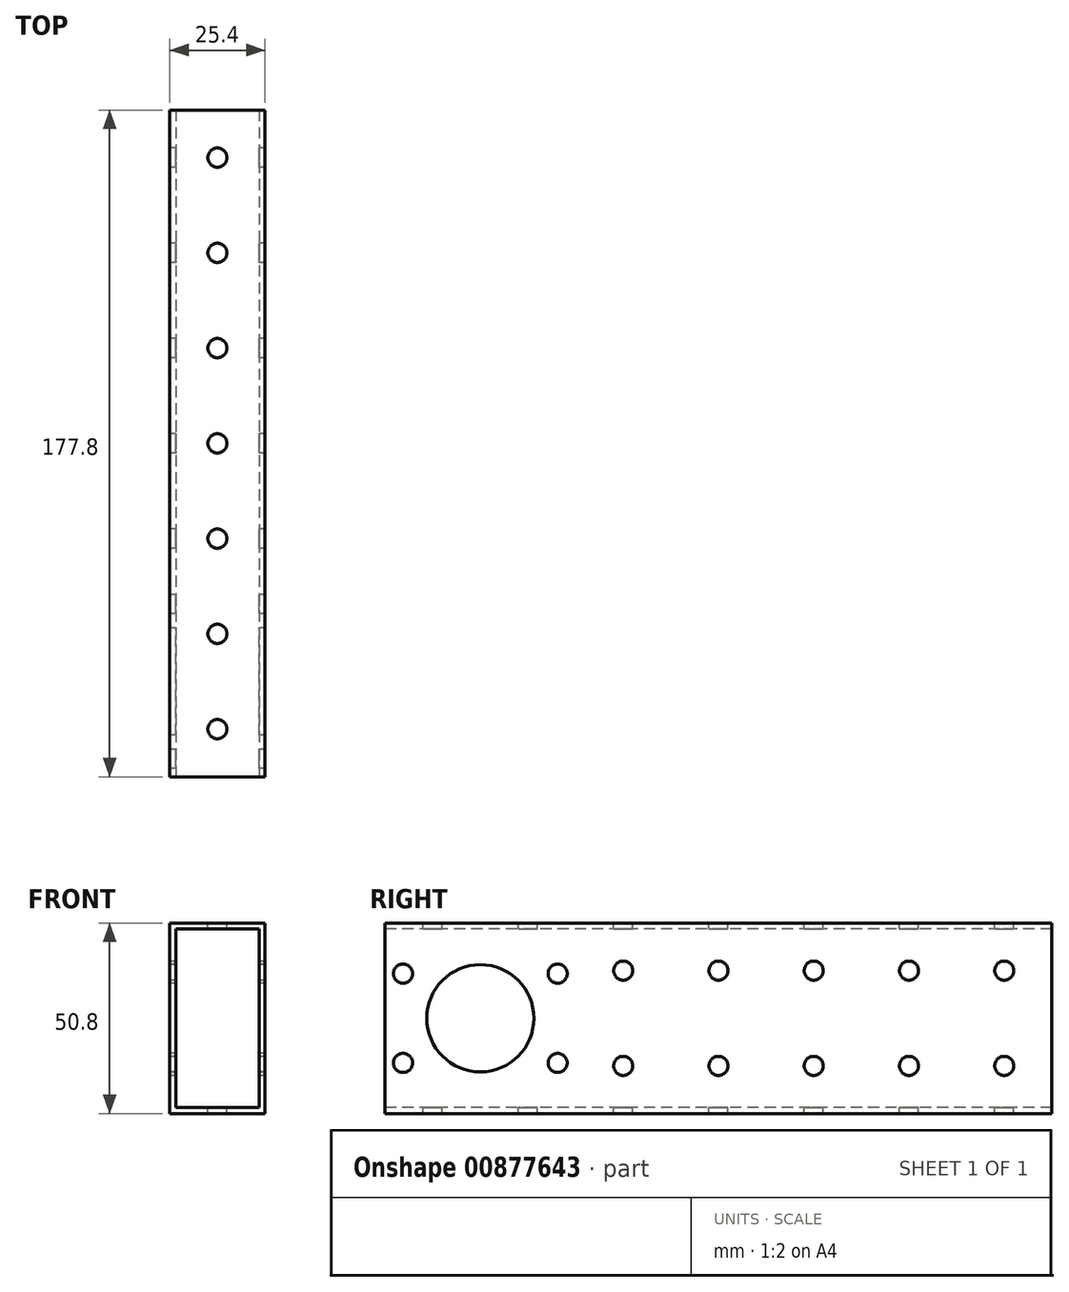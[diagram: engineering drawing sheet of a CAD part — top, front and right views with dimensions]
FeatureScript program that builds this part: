
annotation { "Feature Type Name" : "Feature", "Feature Type Description" : "" }
export const myFeature = defineFeature(function(context is Context, id is Id, definition is map)
    precondition{}
    {
        {
            var Q0;
            Q0=qCreatedBy(makeId("Right.planeOp"),FACE);
            var sketch = newSketch(context, id + "F0", { "sketchPlane" : qUnion([Q0])});
            skLineSegment(sketch, "E0.bottom", {"start": v(-88.9, 25.4) * mm, "end": v(88.9, 25.4) * mm});
            skLineSegment(sketch, "E0.top", {"start": v(-88.9, -25.4) * mm, "end": v(88.9, -25.4) * mm});
            skLineSegment(sketch, "E0.left", {"start": v(-88.9, 25.4) * mm, "end": v(-88.9, -25.4) * mm});
            skLineSegment(sketch, "E0.right", {"start": v(88.9, 25.4) * mm, "end": v(88.9, -25.4) * mm});
            skPoint(sketch, "E0.middle", {"position": v(0, 0) * mm});
            skCircle(sketch, "E1", {"center": v(-63.5, 0) * mm, "radius": 23.81 * mm, "construction": true});
            skCircle(sketch, "E2", {"center": v(-63.5, 23.81) * mm, "radius": 2.55 * mm, "construction": true});
            skCircle(sketch, "E3.1.0", {"center": v(-84.12, 11.9) * mm, "radius": 2.55 * mm});
            skCircle(sketch, "E3.2.0", {"center": v(-84.12, -11.9) * mm, "radius": 2.55 * mm});
            skCircle(sketch, "E3.3.0", {"center": v(-63.5, -23.81) * mm, "radius": 2.55 * mm, "construction": true});
            skCircle(sketch, "E3.4.0", {"center": v(-42.88, -11.9) * mm, "radius": 2.55 * mm});
            skCircle(sketch, "E3.5.0", {"center": v(-42.88, 11.9) * mm, "radius": 2.55 * mm});
            skCircle(sketch, "E4", {"center": v(76.2, 12.7) * mm, "radius": 2.55 * mm});
            skCircle(sketch, "E5.0.1.0", {"center": v(76.2, -12.7) * mm, "radius": 2.55 * mm});
            skCircle(sketch, "E5.1.0.0", {"center": v(50.8, 12.7) * mm, "radius": 2.55 * mm});
            skCircle(sketch, "E5.1.1.0", {"center": v(50.8, -12.7) * mm, "radius": 2.55 * mm});
            skCircle(sketch, "E5.2.0.0", {"center": v(25.4, 12.7) * mm, "radius": 2.55 * mm});
            skCircle(sketch, "E5.2.1.0", {"center": v(25.4, -12.7) * mm, "radius": 2.55 * mm});
            skCircle(sketch, "E5.3.0.0", {"center": v(0, 12.7) * mm, "radius": 2.55 * mm});
            skCircle(sketch, "E5.3.1.0", {"center": v(0, -12.7) * mm, "radius": 2.55 * mm});
            skCircle(sketch, "E5.4.0.0", {"center": v(-25.4, 12.7) * mm, "radius": 2.55 * mm});
            skCircle(sketch, "E5.4.1.0", {"center": v(-25.4, -12.7) * mm, "radius": 2.55 * mm});
            skLineSegment(sketch, "E5.direction1", {"start": v(76.2, 12.7) * mm, "end": v(50.8, 12.7) * mm, "construction": true});
            skLineSegment(sketch, "E5.direction2", {"start": v(76.2, 12.7) * mm, "end": v(76.2, -12.7) * mm, "construction": true});
            skCircle(sketch, "E6", {"center": v(-63.5, 0) * mm, "radius": 14.29 * mm});
            skSolve(sketch);
        }
        {
            var Q0;
            Q0 = qSketchRegion(id + "F0", true);
            extrude(context, id + "F1", {"entities" : qUnion([Q0]), "depth" : 25.4 * mm, "offsetDistance" : 25.4 * mm});
        }
        {
            var Q0;
            Q0=makeQuery(id+"F1.opExtrude","SWEPT_FACE",FACE,{"disambiguationData":[OSD([sQuery(id+"F0.wireOp",EDGE,"E0.left")])]});
            var sketch = newSketch(context, id + "F2", { "sketchPlane" : qUnion([Q0])});
            skLineSegment(sketch, "E7.bottom", {"start": v(23.81, 23.81) * mm, "end": v(1.59, 23.81) * mm});
            skLineSegment(sketch, "E7.top", {"start": v(23.81, -23.81) * mm, "end": v(1.59, -23.81) * mm});
            skLineSegment(sketch, "E7.left", {"start": v(23.81, 23.81) * mm, "end": v(23.81, -23.81) * mm});
            skLineSegment(sketch, "E7.right", {"start": v(1.59, 23.81) * mm, "end": v(1.59, -23.81) * mm});
            skPoint(sketch, "E7.middle", {"position": v(12.7, 0) * mm});
            skSolve(sketch);
        }
        {
            var Q0;
            Q0 = qSketchRegion(id + "F2", true);
            extrude(context, id + "F3", {"entities" : qUnion([Q0]), "operationType" : NewBodyOperationType.REMOVE, "endBound" : BoundingType.THROUGH_ALL, "oppositeDirection" : true, "depth" : 25.4 * mm, "offsetDistance" : 25.4 * mm});
        }
        {
            var Q0;
            Q0=makeQuery(id+"F1.opExtrude","SWEPT_FACE",FACE,{"disambiguationData":[OSD([sQuery(id+"F0.wireOp",EDGE,"E0.bottom")])]});
            var sketch = newSketch(context, id + "F4", { "sketchPlane" : qUnion([Q0])});
            skCircle(sketch, "E8", {"center": v(12.7, 76.2) * mm, "radius": 2.55 * mm});
            skCircle(sketch, "E9.0.1.0", {"center": v(12.7, 50.8) * mm, "radius": 2.55 * mm});
            skCircle(sketch, "E9.0.2.0", {"center": v(12.7, 25.4) * mm, "radius": 2.55 * mm});
            skCircle(sketch, "E9.0.3.0", {"center": v(12.7, 0) * mm, "radius": 2.55 * mm});
            skCircle(sketch, "E9.0.4.0", {"center": v(12.7, -25.4) * mm, "radius": 2.55 * mm});
            skCircle(sketch, "E9.0.5.0", {"center": v(12.7, -50.8) * mm, "radius": 2.55 * mm});
            skCircle(sketch, "E9.0.6.0", {"center": v(12.7, -76.2) * mm, "radius": 2.55 * mm});
            skCircle(sketch, "E9.0.7.0", {"center": v(12.7, -101.6) * mm, "radius": 2.55 * mm});
            skCircle(sketch, "E9.0.8.0", {"center": v(12.7, -127) * mm, "radius": 2.55 * mm});
            skLineSegment(sketch, "E9.direction1", {"start": v(12.7, 76.2) * mm, "end": v(38.1, 76.2) * mm, "construction": true});
            skLineSegment(sketch, "E9.direction2", {"start": v(12.7, 76.2) * mm, "end": v(12.7, 50.8) * mm, "construction": true});
            skSolve(sketch);
        }
        {
            var Q0;
            Q0 = qSketchRegion(id + "F4", true);
            extrude(context, id + "F5", {"entities" : qUnion([Q0]), "operationType" : NewBodyOperationType.REMOVE, "endBound" : BoundingType.THROUGH_ALL, "oppositeDirection" : true, "depth" : 25.4 * mm, "offsetDistance" : 25.4 * mm});
        }
    });
